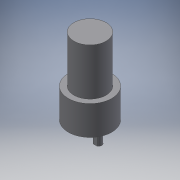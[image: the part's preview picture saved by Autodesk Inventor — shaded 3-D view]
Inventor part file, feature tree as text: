
AUTODESK INVENTOR PART (.ipt)
format: ipt  version: 2017 (Build 210142000, 142)  size: 139,776 bytes
history: native  units: mm
features: other x6, sketch x6, extrude x5, hole x1
ambient origin geometry x8: Origin, YZ Plane, XZ Plane, XY Plane, X Axis, Y Axis, Z Axis, Center Point
bodies: Body1 (feature_tree)
feature tree (18):
  other  "ソリッド1"
  extrude  "押し出し1"  Depth=37.0mm
  extrude  "押し出し2"  Depth=25.0mm TaperAngle=0.0deg
  extrude  "押し出し3"  Depth=27.5mm
  extrude  "押し出し4"  Depth=40.0mm TaperAngle=0.0deg
  hole  "Hole1"  [1 undecoded]
  other  "作業点1"
  other  "作業点2"
  other  "作業平面1"
  extrude  "押し出し5"  Depth=7.0mm
  sketch  "スケッチ1"
  sketch  "スケッチ2"
  sketch  "スケッチ3"
  sketch  "スケッチ4"
  sketch  "スケッチ5"
  other  "作業点3"
  other  "作業点4"
  sketch  "スケッチ6"
note: 1 required parameter value undecoded (feature->parameter linkage not recoverable at this tier; creation-order binding heuristic only, values carry confidence <= 0.55)
